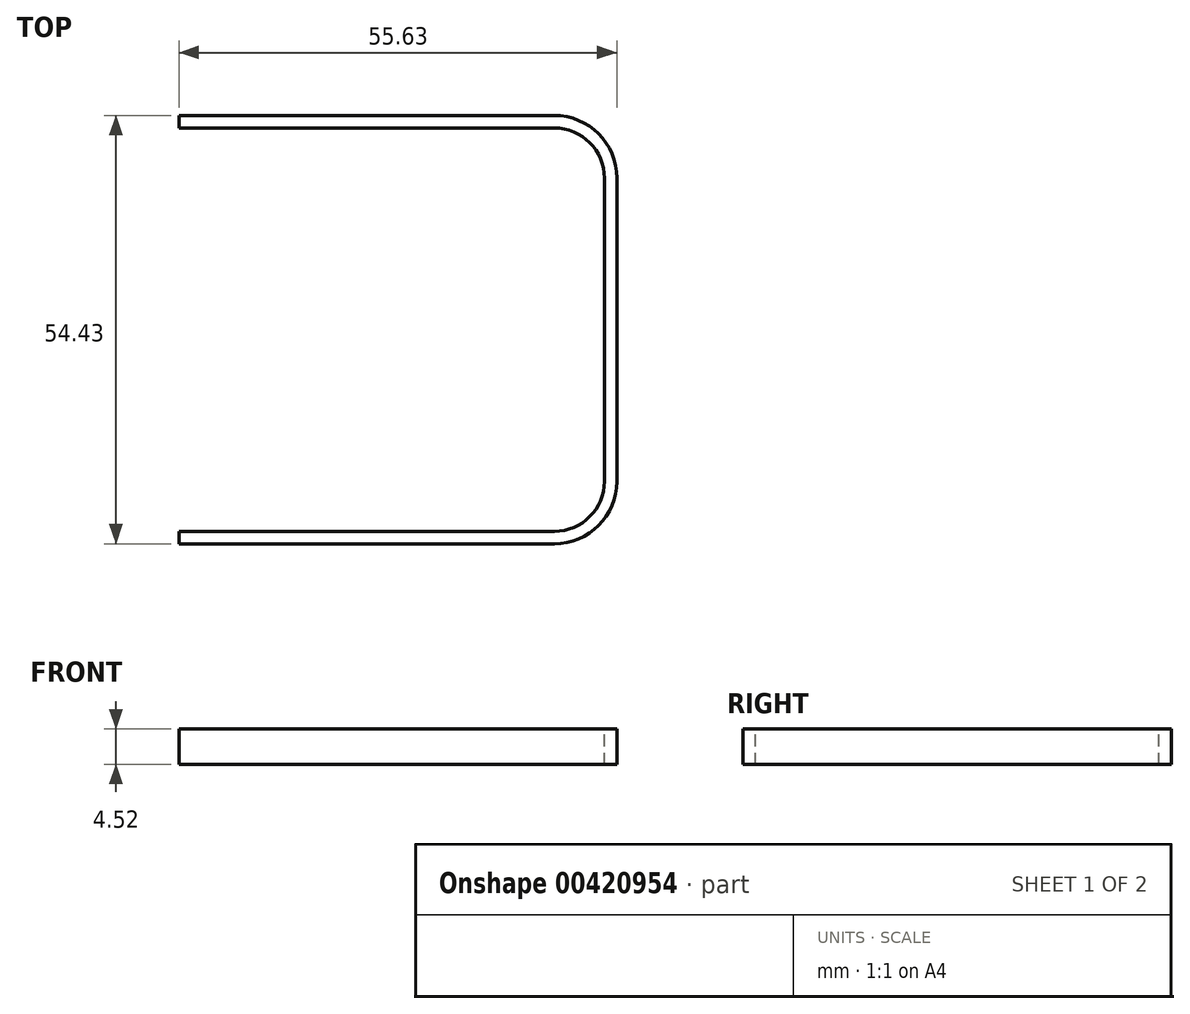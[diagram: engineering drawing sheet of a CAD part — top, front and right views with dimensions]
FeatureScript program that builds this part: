
annotation { "Feature Type Name" : "Feature", "Feature Type Description" : "" }
export const myFeature = defineFeature(function(context is Context, id is Id, definition is map)
    precondition{}
    {
        {
            var Q0;
            Q0=qCreatedBy(makeId("Top.planeOp"),FACE);
            var sketch = newSketch(context, id + "F0", { "sketchPlane" : qUnion([Q0])});
            skLineSegment(sketch, "E0", {"start": v(0, 0) * mm, "end": v(47.7, 0) * mm});
            skLineSegment(sketch, "E1", {"start": v(54.04, 6.35) * mm, "end": v(54.04, 44.9) * mm});
            skLineSegment(sketch, "E2", {"start": v(47.7, 51.25) * mm, "end": v(0, 51.25) * mm});
            skPoint(sketch, "E3.visualSharp", {"position": v(54.04, 0) * mm});
            skArc(sketch, "E3.filletArc", {"start": v(47.7, 0) * mm, "mid": v(52.18, 1.86) * mm, "end": v(54.04, 6.35) * mm});
            skPoint(sketch, "E4.visualSharp", {"position": v(54.04, 51.25) * mm});
            skArc(sketch, "E4.filletArc", {"start": v(54.04, 44.9) * mm, "mid": v(52.18, 49.39) * mm, "end": v(47.7, 51.25) * mm});
            skSolve(sketch);
        }
        {
            var Q0;
            Q0=qCreatedBy(makeId("Right.planeOp"),FACE);
            var sketch = newSketch(context, id + "F1", { "sketchPlane" : qUnion([Q0])});
            skLineSegment(sketch, "E5.bottom", {"start": v(0, 0) * mm, "end": v(-1.59, 0) * mm});
            skLineSegment(sketch, "E5.top", {"start": v(0, 4.52) * mm, "end": v(-1.59, 4.52) * mm});
            skLineSegment(sketch, "E5.left", {"start": v(0, 0) * mm, "end": v(0, 4.52) * mm});
            skLineSegment(sketch, "E5.right", {"start": v(-1.59, 0) * mm, "end": v(-1.59, 4.52) * mm});
            skSolve(sketch);
        }
        {
            var Q0;
            Q0=makeQuery(id+"F1.imprint","IMPRINT",FACE,{"disambiguationData":[TD([[makeQuery(id+"F1.imprint","IMPRINT",EDGE,{"derivedFrom":sQuery(id+"F1.wireOp",EDGE,"E5.bottom")}),-1.0]])]});
            var Q1;
            Q1=sQuery(id+"F0.wireOp",EDGE,"E0");
            var Q2;
            Q2=sQuery(id+"F0.wireOp",EDGE,"E3.filletArc");
            var Q3;
            Q3=sQuery(id+"F0.wireOp",EDGE,"E1");
            var Q4;
            Q4=sQuery(id+"F0.wireOp",EDGE,"E4.filletArc");
            var Q5;
            Q5=sQuery(id+"F0.wireOp",EDGE,"E2");
            sweep(context, id + "F2", {"profiles" : qUnion([Q0]), "path" : qUnion([Q1, Q2, Q3, Q4, Q5])});
        }
    });
